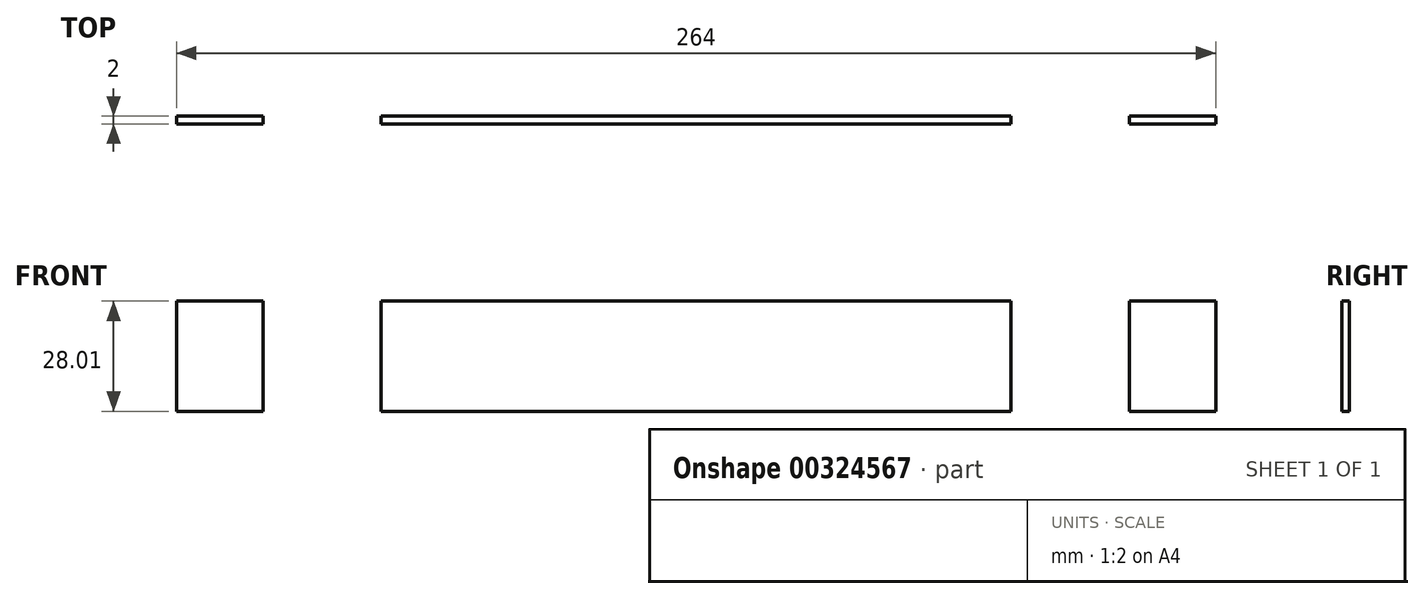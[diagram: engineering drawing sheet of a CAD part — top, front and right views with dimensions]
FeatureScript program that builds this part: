
annotation { "Feature Type Name" : "Feature", "Feature Type Description" : "" }
export const myFeature = defineFeature(function(context is Context, id is Id, definition is map)
    precondition{}
    {
        {
            var Q0;
            Q0=qCreatedBy(makeId("Front.planeOp"),FACE);
            var sketch = newSketch(context, id + "F0", { "sketchPlane" : qUnion([Q0])});
            skLineSegment(sketch, "E0.bottom", {"start": v(-82.37, -9.07) * mm, "end": v(73.63, -9.07) * mm});
            skLineSegment(sketch, "E0.top", {"start": v(-82.37, 6.93) * mm, "end": v(73.63, 6.93) * mm});
            skLineSegment(sketch, "E0.left", {"start": v(-82.37, -9.07) * mm, "end": v(-82.37, 6.93) * mm});
            skLineSegment(sketch, "E0.right", {"start": v(73.63, -9.07) * mm, "end": v(73.63, 6.93) * mm});
            skLineSegment(sketch, "E1.top", {"start": v(-136.37, 16.93) * mm, "end": v(127.63, 16.93) * mm});
            skLineSegment(sketch, "E2", {"start": v(-136.37, -11.08) * mm, "end": v(127.63, -11.08) * mm});
            skLineSegment(sketch, "E3", {"start": v(105.63, 16.93) * mm, "end": v(105.63, -11.08) * mm});
            skLineSegment(sketch, "E4", {"start": v(75.63, 16.93) * mm, "end": v(75.63, -11.08) * mm});
            skLineSegment(sketch, "E5", {"start": v(-114.37, 16.93) * mm, "end": v(-114.37, -11.08) * mm});
            skLineSegment(sketch, "E6", {"start": v(-84.37, 16.93) * mm, "end": v(-84.37, -11.08) * mm});
            skLineSegment(sketch, "E7.right", {"start": v(-136.37, 16.93) * mm, "end": v(-136.37, -11.08) * mm});
            skLineSegment(sketch, "E8.right", {"start": v(127.63, 16.93) * mm, "end": v(127.63, -11.08) * mm});
            skSolve(sketch);
        }
        {
            var Q0;
            Q0=makeQuery(id+"F0.imprint","IMPRINT",FACE,{"disambiguationData":[TD([[makeQuery(id+"F0.imprint","IMPRINT",EDGE,{"derivedFrom":sQuery(id+"F0.wireOp",EDGE,"E0.bottom")}),-1.0]])]});
            var Q1;
            Q1=makeQuery(id+"F0.imprint","IMPRINT",FACE,{"disambiguationData":[TD([[makeQuery(id+"F0.imprint","IMPRINT",EDGE,{"derivedFrom":sQuery(id+"F0.wireOp",EDGE,"E0.bottom")}),1.0]])]});
            extrude(context, id + "F1", {"entities" : qUnion([Q0, Q1]), "depth" : 2 * mm});
        }
        {
            var Q0;
            {var subQ4=sQuery(id+"F0.wireOp",EDGE,"E3");Q0=makeQuery(id+"F0.imprint","IMPRINT",FACE,{"disambiguationData":[TD([[makeQuery(id+"F0.imprint","IMPRINT",EDGE,{"derivedFrom":subQ4}),1.0]])]});}
            var Q1;
            {var subQ1=sQuery(id+"F0.wireOp",EDGE,"c064692c-e3e0-441b-b867-f38e62f1c33a");Q1=makeQuery(id+"F0.imprint","IMPRINT",FACE,{"disambiguationData":[TD([[makeQuery(id+"F0.imprint","IMPRINT",EDGE,{"derivedFrom":subQ1}),-1.0]])]});}
            extrude(context, id + "F2", {"entities" : qUnion([Q0, Q1]), "depth" : 2 * mm});
        }
        {
            var Q0;
            {var subQ2=sQuery(id+"F0.wireOp",EDGE,"E5");Q0=makeQuery(id+"F0.imprint","IMPRINT",FACE,{"disambiguationData":[TD([[makeQuery(id+"F0.imprint","IMPRINT",EDGE,{"derivedFrom":subQ2}),-1.0]])]});}
            extrude(context, id + "F3", {"entities" : qUnion([Q0]), "depth" : 2 * mm});
        }
    });
